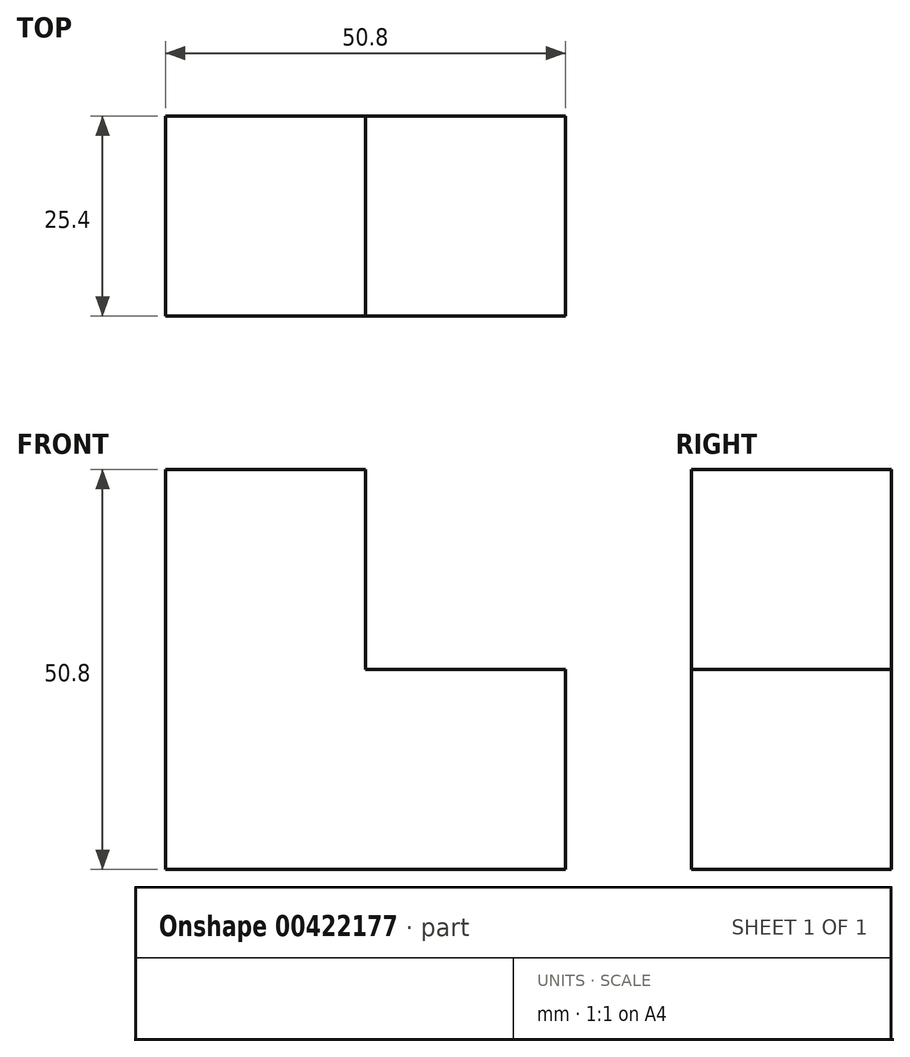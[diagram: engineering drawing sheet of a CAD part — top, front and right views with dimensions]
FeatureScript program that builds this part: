
annotation { "Feature Type Name" : "Feature", "Feature Type Description" : "" }
export const myFeature = defineFeature(function(context is Context, id is Id, definition is map)
    precondition{}
    {
        {
            var Q0;
            Q0=qCreatedBy(makeId("Front.planeOp"),FACE);
            var sketch = newSketch(context, id + "F0", { "sketchPlane" : qUnion([Q0])});
            skLineSegment(sketch, "E0.bottom", {"start": v(0, 0) * mm, "end": v(-25.4, 0) * mm});
            skLineSegment(sketch, "E0.top", {"start": v(0, 50.8) * mm, "end": v(-25.4, 50.8) * mm});
            skLineSegment(sketch, "E0.left", {"start": v(0, 0) * mm, "end": v(0, 50.8) * mm});
            skLineSegment(sketch, "E0.right", {"start": v(-25.4, 0) * mm, "end": v(-25.4, 50.8) * mm});
            skLineSegment(sketch, "E1.bottom", {"start": v(0, 0) * mm, "end": v(25.4, 0) * mm});
            skLineSegment(sketch, "E1.top", {"start": v(0, 25.4) * mm, "end": v(25.4, 25.4) * mm});
            skLineSegment(sketch, "E1.left", {"start": v(0, 0) * mm, "end": v(0, 25.4) * mm});
            skLineSegment(sketch, "E1.right", {"start": v(25.4, 0) * mm, "end": v(25.4, 25.4) * mm});
            skSolve(sketch);
        }
        {
            var Q0;
            Q0 = qSketchRegion(id + "F0", true);
            extrude(context, id + "F1", {"entities" : qUnion([Q0]), "depth" : 25.4 * mm});
        }
    });
